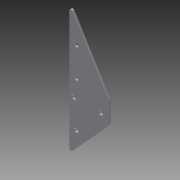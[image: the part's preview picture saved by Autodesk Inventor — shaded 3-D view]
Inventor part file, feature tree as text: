
AUTODESK INVENTOR PART (.ipt)
format: ipt  version: 2014 SP1 (Build 180222100, 222)  size: 125,440 bytes
history: native  units: in
note: dims shown in document units (in); Inventor stores cm internally (conversion verified against a paired STEP export)
features: extrude x5, sketch x5, fillet x3
ambient origin geometry x8: Origin, YZ Plane, XZ Plane, XY Plane, X Axis, Y Axis, Z Axis, Center Point
bodies: Solid1 (feature_tree)
feature tree (13):
  extrude  "Extrusion1"  Depth=6.0in
  extrude  "Extrusion2"  Depth=0.125in
  fillet  "Fillet1"  Radius=0.28in
  extrude  "Extrusion3"  Depth=0.5in
  fillet  "Fillet2"  Radius=0.56in
  fillet  "Fillet3"  Radius=0.31in
  extrude  "Extrusion4"  Depth=0.125in
  extrude  "Extrusion5"  Depth=0.125in
  sketch  "Sketch1"  dims[d1=1.5in d2=6.0in]
  sketch  "Sketch2"  dims[d3=0.125in d4=0.0in d5=0.28in d6=0.28in]
  sketch  "Sketch3"  dims[d7=0.5in d8=0.5in d9=0.56in d11=0.31in]
  sketch  "Sketch4"  dims[d12=1.0in d13=0.0in d14=0.125in]
  sketch  "Sketch5"  dims[d15=0.266in d16=0.266in d17=0.5in d18=0.5in d19=1.737in d20=2.0in d21=1.0in d22=0.0in d23=0.125in d24=3.0in d25=2.75in d26=2.75in d27=0.125in d28=0.266in d29=3.125in d30=0.5in d31=1.0in d32=0.0in d33=1.0in d34=0.0in]
